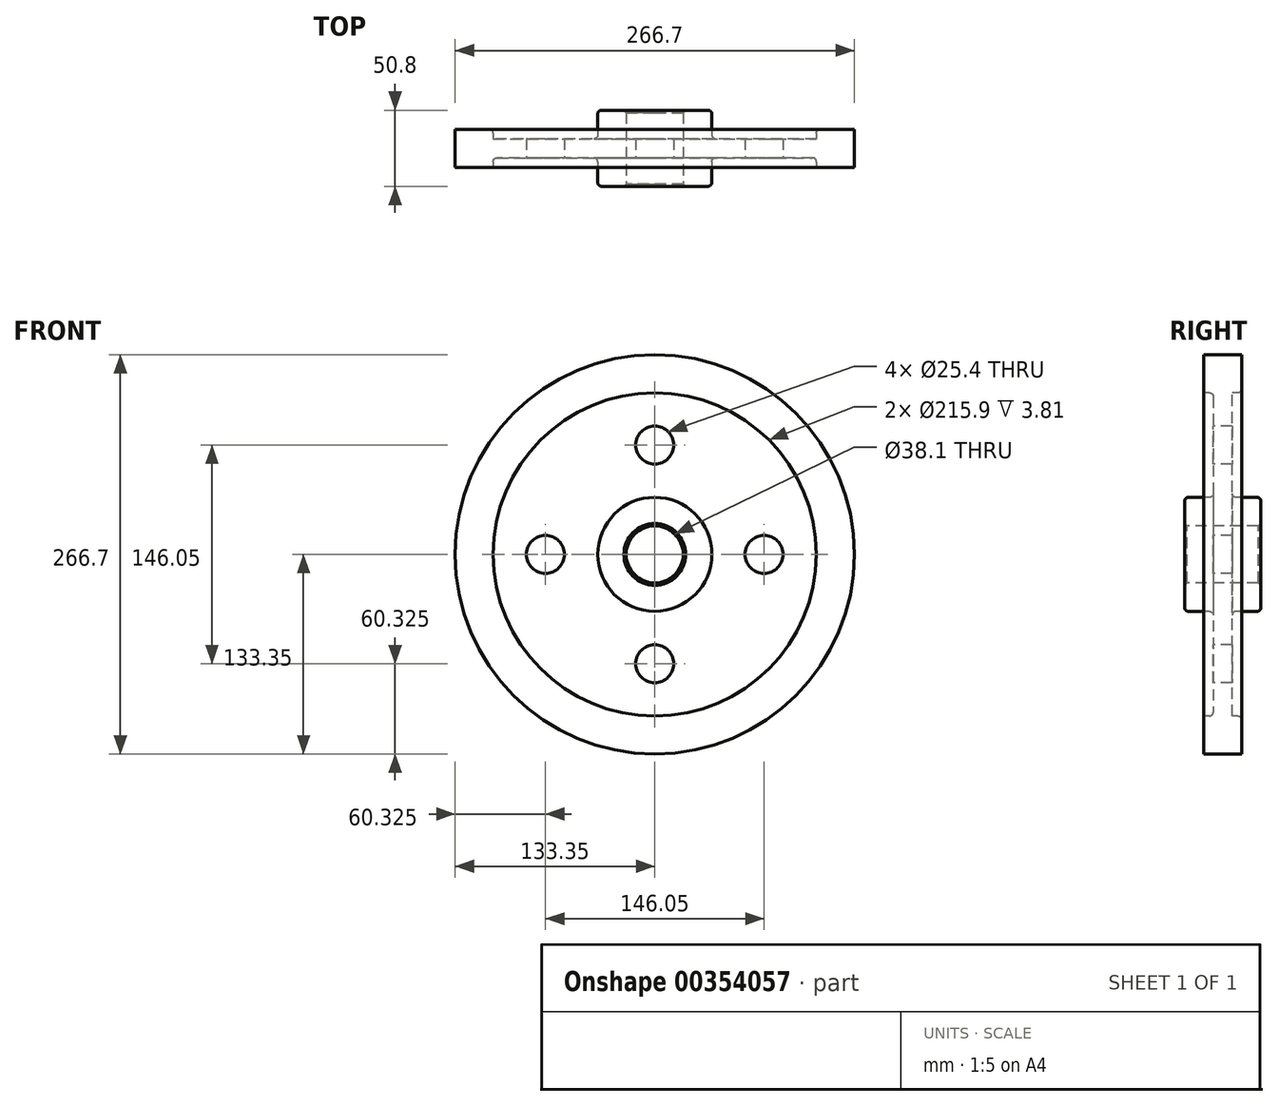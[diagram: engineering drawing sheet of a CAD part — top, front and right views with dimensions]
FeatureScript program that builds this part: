
annotation { "Feature Type Name" : "Feature", "Feature Type Description" : "" }
export const myFeature = defineFeature(function(context is Context, id is Id, definition is map)
    precondition{}
    {
        {
            var Q0;
            Q0=qCreatedBy(makeId("Right.planeOp"),FACE);
            var sketch = newSketch(context, id + "F0", { "sketchPlane" : qUnion([Q0])});
            skLineSegment(sketch, "E0", {"start": v(0, 0) * mm, "end": v(25.4, 0) * mm, "construction": true});
            skLineSegment(sketch, "E1.0", {"start": v(0, 133.35) * mm, "end": v(12.7, 133.35) * mm});
            skLineSegment(sketch, "E2", {"start": v(0, 133.35) * mm, "end": v(0, 0) * mm});
            skLineSegment(sketch, "E3.0", {"start": v(12.7, 133.35) * mm, "end": v(12.7, 107.95) * mm});
            skLineSegment(sketch, "E4.trimOffspring", {"start": v(12.7, 19.05) * mm, "end": v(12.7, 0) * mm});
            skLineSegment(sketch, "E5.bottom", {"start": v(12.7, 19.05) * mm, "end": v(25.4, 19.05) * mm});
            skLineSegment(sketch, "E5.top", {"start": v(12.7, 38.1) * mm, "end": v(25.4, 38.1) * mm});
            skLineSegment(sketch, "E5.left", {"start": v(0, 19.05) * mm, "end": v(0, 38.1) * mm});
            skLineSegment(sketch, "E5.right", {"start": v(25.4, 19.05) * mm, "end": v(25.4, 38.1) * mm});
            skLineSegment(sketch, "E6", {"start": v(12.7, 107.95) * mm, "end": v(6.35, 107.95) * mm});
            skLineSegment(sketch, "E7", {"start": v(6.35, 107.95) * mm, "end": v(6.35, 38.1) * mm});
            skLineSegment(sketch, "E8", {"start": v(6.35, 38.1) * mm, "end": v(12.7, 38.1) * mm});
            skLineSegment(sketch, "E9", {"start": v(12.7, 19.05) * mm, "end": v(0, 19.05) * mm});
            skLineSegment(sketch, "E10.MirrorCS", {"start": v(0, 133.35) * mm, "end": v(-12.7, 133.35) * mm});
            skLineSegment(sketch, "E11.MirrorCS", {"start": v(-12.7, 133.35) * mm, "end": v(-12.7, 107.95) * mm});
            skLineSegment(sketch, "E12.MirrorCS", {"start": v(-6.35, 107.95) * mm, "end": v(-6.35, 38.1) * mm});
            skLineSegment(sketch, "E13.MirrorCS", {"start": v(-12.7, 107.95) * mm, "end": v(-6.35, 107.95) * mm});
            skLineSegment(sketch, "E14.MirrorCS", {"start": v(-6.35, 38.1) * mm, "end": v(-12.7, 38.1) * mm});
            skLineSegment(sketch, "E15.MirrorCS", {"start": v(-12.7, 38.1) * mm, "end": v(-25.4, 38.1) * mm});
            skLineSegment(sketch, "E16.MirrorCS", {"start": v(-25.4, 19.05) * mm, "end": v(-25.4, 38.1) * mm});
            skLineSegment(sketch, "E17.MirrorCS", {"start": v(-12.7, 19.05) * mm, "end": v(-25.4, 19.05) * mm});
            skLineSegment(sketch, "E18.MirrorCS", {"start": v(-12.7, 19.05) * mm, "end": v(0, 19.05) * mm});
            skSolve(sketch);
        }
        {
            var Q0;
            Q0 = qSketchRegion(id + "F0", true);
            var Q1;
            Q1=sQuery(id+"F0.wireOp",EDGE,"E0");
            revolve(context, id + "F1", {"entities" : qUnion([Q0]), "axis" : qUnion([Q1]), "revolveType" : RevolveType.FULL});
        }
        {
            var Q0;
            Q0=makeQuery(id+"F1.opRevolve","SWEPT_FACE",FACE,{"disambiguationData":[OSD([sQuery(id+"F0.wireOp",EDGE,"E12.MirrorCS")])]});
            var sketch = newSketch(context, id + "F2", { "sketchPlane" : qUnion([Q0])});
            skLineSegment(sketch, "E19", {"start": v(0, 0) * mm, "end": v(0, 73.03) * mm});
            skCircle(sketch, "E20", {"center": v(0, 73.03) * mm, "radius": 12.7 * mm});
            skCircle(sketch, "E21.1.0", {"center": v(-73.03, 0) * mm, "radius": 12.7 * mm});
            skCircle(sketch, "E21.2.0", {"center": v(0, -73.03) * mm, "radius": 12.7 * mm});
            skCircle(sketch, "E21.3.0", {"center": v(73.03, 0) * mm, "radius": 12.7 * mm});
            skPoint(sketch, "E21.center", {"position": v(0, 0) * mm});
            skSolve(sketch);
        }
        {
            var Q0;
            Q0=makeQuery(id+"F2.imprint","IMPRINT",FACE,{"disambiguationData":[TD([[makeQuery(id+"F2.imprint","IMPRINT",EDGE,{"derivedFrom":sQuery(id+"F2.wireOp",EDGE,"E20")}),1.0]])]});
            var Q1;
            Q1=makeQuery(id+"F2.imprint","IMPRINT",FACE,{"disambiguationData":[TD([[makeQuery(id+"F2.imprint","IMPRINT",EDGE,{"derivedFrom":sQuery(id+"F2.wireOp",EDGE,"E21.3.0")}),1.0]])]});
            var Q2;
            Q2=makeQuery(id+"F2.imprint","IMPRINT",FACE,{"disambiguationData":[TD([[makeQuery(id+"F2.imprint","IMPRINT",EDGE,{"derivedFrom":sQuery(id+"F2.wireOp",EDGE,"E21.2.0")}),1.0]])]});
            var Q3;
            Q3=makeQuery(id+"F2.imprint","IMPRINT",FACE,{"disambiguationData":[TD([[makeQuery(id+"F2.imprint","IMPRINT",EDGE,{"derivedFrom":sQuery(id+"F2.wireOp",EDGE,"E21.1.0")}),1.0]])]});
            extrude(context, id + "F3", {"entities" : qUnion([Q0, Q1, Q2, Q3]), "operationType" : NewBodyOperationType.REMOVE, "oppositeDirection" : true, "depth" : 25.4 * mm});
        }
        {
            var Q0;
            Q0=makeQuery(id+"F1.opRevolve","SWEPT_EDGE",EDGE,{"disambiguationData":[OSD([sQuery(id+"F0.wireOp",EDGE,"E12.MirrorCS"),sQuery(id+"F0.wireOp",EDGE,"E13.MirrorCS")])]});
            var Q1;
            Q1=makeQuery(id+"F1.opRevolve","SWEPT_EDGE",EDGE,{"disambiguationData":[OSD([sQuery(id+"F0.wireOp",EDGE,"E12.MirrorCS"),sQuery(id+"F0.wireOp",EDGE,"E14.MirrorCS")])]});
            var Q2;
            Q2=makeQuery(id+"F1.opRevolve","SWEPT_EDGE",EDGE,{"disambiguationData":[OSD([sQuery(id+"F0.wireOp",EDGE,"E15.MirrorCS"),sQuery(id+"F0.wireOp",EDGE,"E16.MirrorCS")])]});
            var Q3;
            Q3=makeQuery(id+"F1.opRevolve","SWEPT_EDGE",EDGE,{"disambiguationData":[OSD([sQuery(id+"F0.wireOp",EDGE,"E7"),sQuery(id+"F0.wireOp",EDGE,"E8")])]});
            var Q4;
            Q4=makeQuery(id+"F1.opRevolve","SWEPT_EDGE",EDGE,{"disambiguationData":[OSD([sQuery(id+"F0.wireOp",EDGE,"E5.top"),sQuery(id+"F0.wireOp",EDGE,"E5.right")])]});
            var Q5;
            Q5=makeQuery(id+"F1.opRevolve","SWEPT_EDGE",EDGE,{"disambiguationData":[OSD([sQuery(id+"F0.wireOp",EDGE,"E3.0"),sQuery(id+"F0.wireOp",EDGE,"E6")])]});
            fillet(context, id + "F4", {"entities" : qUnion([Q0, Q1, Q2, Q3, Q4, Q5]), "radius" : 2.54 * mm, "tangentPropagation" : true, "allowEdgeOverflow" : false});
        }
        {
            var Q0;
            Q0=makeQuery(id+"F1.opRevolve","SWEPT_EDGE",EDGE,{"disambiguationData":[OSD([sQuery(id+"F0.wireOp",EDGE,"E5.bottom"),sQuery(id+"F0.wireOp",EDGE,"E5.right")])]});
            var Q1;
            Q1=makeQuery(id+"F1.opRevolve","SWEPT_EDGE",EDGE,{"disambiguationData":[OSD([sQuery(id+"F0.wireOp",EDGE,"E16.MirrorCS"),sQuery(id+"F0.wireOp",EDGE,"E17.MirrorCS")])]});
            chamfer(context, id + "F5", {"entities" : qUnion([Q0, Q1]), "width" : 1.59 * mm, "tangentPropagation" : true});
        }
    });
